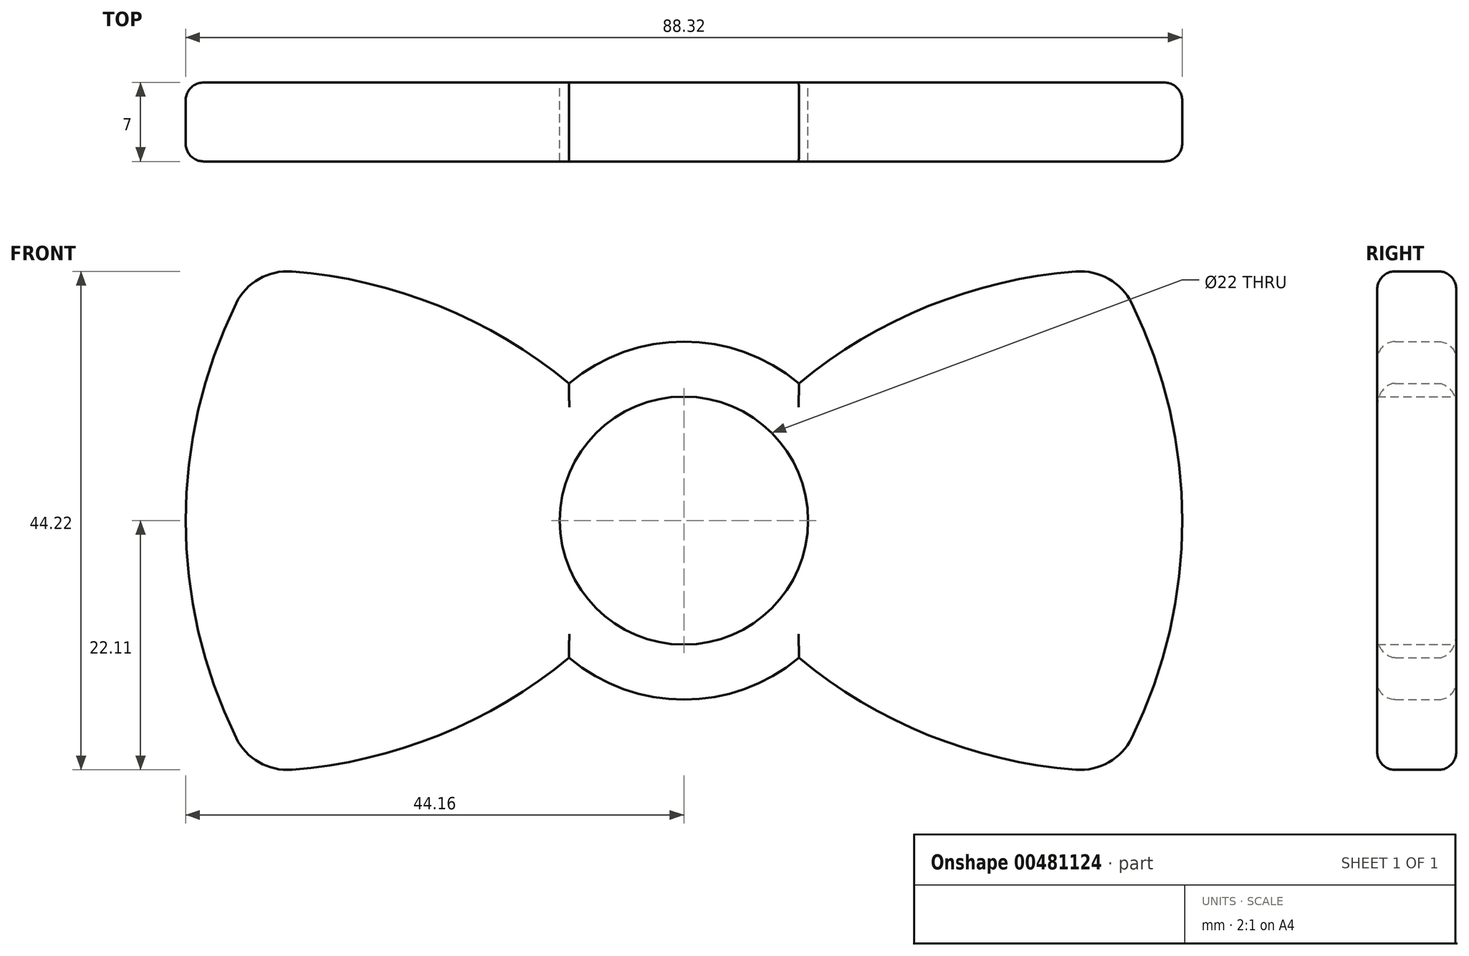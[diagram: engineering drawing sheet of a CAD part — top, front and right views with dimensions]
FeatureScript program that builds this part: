
annotation { "Feature Type Name" : "Feature", "Feature Type Description" : "" }
export const myFeature = defineFeature(function(context is Context, id is Id, definition is map)
    precondition{}
    {
        {
            var Q0;
            Q0=qCreatedBy(makeId("Front.planeOp"),FACE);
            var sketch = newSketch(context, id + "F0", { "sketchPlane" : qUnion([Q0])});
            skLineSegment(sketch, "E0.bottom", {"start": v(38.1, 22.22) * mm, "end": v(-38.1, 22.23) * mm, "construction": true});
            skLineSegment(sketch, "E0.top", {"start": v(38.1, -22.23) * mm, "end": v(-38.1, -22.23) * mm, "construction": true});
            skLineSegment(sketch, "E0.left", {"start": v(38.1, 22.22) * mm, "end": v(38.1, -22.23) * mm});
            skLineSegment(sketch, "E0.right", {"start": v(-38.1, 22.23) * mm, "end": v(-38.1, -22.22) * mm, "construction": true});
            skPoint(sketch, "E0.middle", {"position": v(0, 0) * mm});
            skLineSegment(sketch, "E1", {"start": v(-38.1, 22.23) * mm, "end": v(38.1, -22.23) * mm, "construction": true});
            skLineSegment(sketch, "E2", {"start": v(38.1, 22.23) * mm, "end": v(-38.1, -22.22) * mm, "construction": true});
            skCircle(sketch, "E3", {"center": v(0, 0) * mm, "radius": 15.88 * mm});
            skLineSegment(sketch, "E4", {"start": v(0, 48.06) * mm, "end": v(0, -55.54) * mm, "construction": true});
            skLineSegment(sketch, "E5", {"start": v(-90.95, 0) * mm, "end": v(91.81, 0) * mm, "construction": true});
            skArc(sketch, "E6", {"start": v(-38.1, 22.23) * mm, "mid": v(-44.16, 0) * mm, "end": v(-38.1, -22.23) * mm});
            skArc(sketch, "E7", {"start": v(-38.1, -22.22) * mm, "mid": v(-16.05, -16.26) * mm, "end": v(0, 0) * mm});
            skArc(sketch, "E8", {"start": v(0, 0) * mm, "mid": v(-16.05, 16.26) * mm, "end": v(-38.1, 22.23) * mm});
            skArc(sketch, "E9", {"start": v(38.1, 22.23) * mm, "mid": v(16.05, 16.26) * mm, "end": v(0, 0) * mm});
            skArc(sketch, "E10", {"start": v(38.1, -22.23) * mm, "mid": v(44.16, 0) * mm, "end": v(38.1, 22.22) * mm});
            skArc(sketch, "E11", {"start": v(0, 0) * mm, "mid": v(16.05, -16.26) * mm, "end": v(38.1, -22.23) * mm});
            skSolve(sketch);
        }
        {
            var Q0;
            {var subQ5=sQuery(id+"F0.wireOp",EDGE,"E6");Q0=makeQuery(id+"F0.imprint","IMPRINT",FACE,{"disambiguationData":[TD([[makeQuery(id+"F0.imprint","IMPRINT",EDGE,{"derivedFrom":subQ5}),1.0]])]});}
            var Q1;
            {var subQ0=sQuery(id+"F0.wireOp",EDGE,"E8");var subQ1=sQuery(id+"F0.wireOp",EDGE,"E3");var subQ2=makeQuery(id+"F0.imprint","INTERSECT",VERTEX,{"derivedFrom":[subQ1,subQ0]});Q1=makeQuery(id+"F0.imprint","IMPRINT",FACE,{"disambiguationData":[TD([[makeQuery(id+"F0.imprint","IMPRINT",EDGE,{"disambiguationData":[TD([[subQ2,-1.0]])],"derivedFrom":subQ1}),1.0]])]});}
            var Q2;
            {var subQ0=sQuery(id+"F0.wireOp",EDGE,"E8");var subQ1=sQuery(id+"F0.wireOp",EDGE,"E3");var subQ2=makeQuery(id+"F0.imprint","INTERSECT",VERTEX,{"derivedFrom":[subQ1,subQ0]});Q2=makeQuery(id+"F0.imprint","IMPRINT",FACE,{"disambiguationData":[TD([[makeQuery(id+"F0.imprint","IMPRINT",EDGE,{"disambiguationData":[TD([[subQ2,1.0]])],"derivedFrom":subQ1}),1.0]])]});}
            var Q3;
            {var subQ0=sQuery(id+"F0.wireOp",EDGE,"E7");var subQ1=sQuery(id+"F0.wireOp",EDGE,"E3");var subQ2=makeQuery(id+"F0.imprint","INTERSECT",VERTEX,{"derivedFrom":[subQ1,subQ0]});Q3=makeQuery(id+"F0.imprint","IMPRINT",FACE,{"disambiguationData":[TD([[makeQuery(id+"F0.imprint","IMPRINT",EDGE,{"disambiguationData":[TD([[subQ2,-1.0]])],"derivedFrom":subQ1}),1.0]])]});}
            var Q4;
            {var subQ0=sQuery(id+"F0.wireOp",EDGE,"E9");var subQ1=sQuery(id+"F0.wireOp",EDGE,"E3");var subQ2=makeQuery(id+"F0.imprint","INTERSECT",VERTEX,{"derivedFrom":[subQ1,subQ0]});Q4=makeQuery(id+"F0.imprint","IMPRINT",FACE,{"disambiguationData":[TD([[makeQuery(id+"F0.imprint","IMPRINT",EDGE,{"disambiguationData":[TD([[subQ2,1.0]])],"derivedFrom":subQ1}),1.0]])]});}
            var Q5;
            {var subQ0=sQuery(id+"F0.wireOp",EDGE,"E0.left");Q5=makeQuery(id+"F0.imprint","IMPRINT",FACE,{"disambiguationData":[TD([[makeQuery(id+"F0.imprint","IMPRINT",EDGE,{"derivedFrom":subQ0}),-1.0]])]});}
            var Q6;
            Q6=makeQuery(id+"F0.imprint","IMPRINT",FACE,{"disambiguationData":[TD([[makeQuery(id+"F0.imprint","IMPRINT",EDGE,{"derivedFrom":sQuery(id+"F0.wireOp",EDGE,"E0.left")}),1.0]])]});
            extrude(context, id + "F1", {"entities" : qUnion([Q0, Q1, Q2, Q3, Q4, Q5, Q6]), "depth" : 7 * mm});
        }
        {
            var Q0;
            Q0=makeQuery(id+"F1.opExtrude","CAP_FACE",FACE,{"disambiguationData":[OSD([sQuery(id+"F0.wireOp",EDGE,"E3"),sQuery(id+"F0.wireOp",EDGE,"E6"),sQuery(id+"F0.wireOp",EDGE,"E7"),sQuery(id+"F0.wireOp",EDGE,"E8"),sQuery(id+"F0.wireOp",EDGE,"E9"),sQuery(id+"F0.wireOp",EDGE,"E10"),sQuery(id+"F0.wireOp",EDGE,"E11")])],"isStart":true});
            var sketch = newSketch(context, id + "F2", { "sketchPlane" : qUnion([Q0])});
            skCircle(sketch, "E12", {"center": v(0, 0) * mm, "radius": 11 * mm});
            skLineSegment(sketch, "E13", {"start": v(0, 36.34) * mm, "end": v(0, -37.6) * mm, "construction": true});
            skLineSegment(sketch, "E14", {"start": v(-26.99, 0) * mm, "end": v(26.99, 0) * mm, "construction": true});
            skCircle(sketch, "E15", {"center": v(-26.99, 0) * mm, "radius": 11 * mm});
            skCircle(sketch, "E16", {"center": v(26.99, 0) * mm, "radius": 11 * mm});
            skSolve(sketch);
        }
        {
            var Q0;
            Q0=makeQuery(id+"F2.imprint","IMPRINT",FACE,{"disambiguationData":[TD([[makeQuery(id+"F2.imprint","IMPRINT",EDGE,{"derivedFrom":sQuery(id+"F2.wireOp",EDGE,"E12")}),1.0]])]});
            extrude(context, id + "F3", {"entities" : qUnion([Q0]), "operationType" : NewBodyOperationType.REMOVE, "endBound" : BoundingType.THROUGH_ALL, "oppositeDirection" : true, "depth" : 25.4 * mm});
        }
        {
            var Q0;
            Q0=makeQuery(id+"F1.opExtrude","CAP_EDGE",EDGE,{"disambiguationData":[OSD([sQuery(id+"F0.wireOp",EDGE,"E6")])],"isStart":false});
            var Q1;
            Q1=makeQuery(id+"F1.opExtrude","CAP_EDGE",EDGE,{"disambiguationData":[OSD([sQuery(id+"F0.wireOp",EDGE,"E7")])],"isStart":false});
            var Q2;
            {var subQ0=sQuery(id+"F0.wireOp",EDGE,"E3");Q2=makeQuery(id+"F1.opExtrude","CAP_EDGE",EDGE,{"disambiguationData":[OSD([subQ0]),TDD([makeQuery(id+"F0.imprint","IMPRINT",EDGE,{"disambiguationData":[TD([[makeQuery(id+"F0.imprint","INTERSECT",VERTEX,{"derivedFrom":[subQ0,sQuery(id+"F0.wireOp",EDGE,"E7")]}),-1.0]])],"derivedFrom":subQ0})])],"isStart":false});}
            var Q3;
            Q3=makeQuery(id+"F1.opExtrude","CAP_EDGE",EDGE,{"disambiguationData":[OSD([sQuery(id+"F0.wireOp",EDGE,"E11")])],"isStart":false});
            var Q4;
            Q4=makeQuery(id+"F1.opExtrude","CAP_EDGE",EDGE,{"disambiguationData":[OSD([sQuery(id+"F0.wireOp",EDGE,"E10")])],"isStart":false});
            var Q5;
            Q5=makeQuery(id+"F1.opExtrude","CAP_EDGE",EDGE,{"disambiguationData":[OSD([sQuery(id+"F0.wireOp",EDGE,"E9")])],"isStart":false});
            var Q6;
            {var subQ0=sQuery(id+"F0.wireOp",EDGE,"E3");Q6=makeQuery(id+"F1.opExtrude","CAP_EDGE",EDGE,{"disambiguationData":[OSD([subQ0]),TDD([makeQuery(id+"F0.imprint","IMPRINT",EDGE,{"disambiguationData":[TD([[makeQuery(id+"F0.imprint","INTERSECT",VERTEX,{"derivedFrom":[subQ0,sQuery(id+"F0.wireOp",EDGE,"E8")]}),1.0]])],"derivedFrom":subQ0})])],"isStart":false});}
            var Q7;
            Q7=makeQuery(id+"F1.opExtrude","CAP_EDGE",EDGE,{"disambiguationData":[OSD([sQuery(id+"F0.wireOp",EDGE,"E8")])],"isStart":false});
            var Q8;
            Q8=makeQuery(id+"F1.opExtrude","CAP_EDGE",EDGE,{"disambiguationData":[OSD([sQuery(id+"F0.wireOp",EDGE,"E8")])],"isStart":true});
            var Q9;
            {var subQ0=sQuery(id+"F0.wireOp",EDGE,"E3");Q9=makeQuery(id+"F1.opExtrude","CAP_EDGE",EDGE,{"disambiguationData":[OSD([subQ0]),TDD([makeQuery(id+"F0.imprint","IMPRINT",EDGE,{"disambiguationData":[TD([[makeQuery(id+"F0.imprint","INTERSECT",VERTEX,{"derivedFrom":[subQ0,sQuery(id+"F0.wireOp",EDGE,"E8")]}),1.0]])],"derivedFrom":subQ0})])],"isStart":true});}
            var Q10;
            Q10=makeQuery(id+"F1.opExtrude","CAP_EDGE",EDGE,{"disambiguationData":[OSD([sQuery(id+"F0.wireOp",EDGE,"E9")])],"isStart":true});
            var Q11;
            Q11=makeQuery(id+"F1.opExtrude","CAP_EDGE",EDGE,{"disambiguationData":[OSD([sQuery(id+"F0.wireOp",EDGE,"E10")])],"isStart":true});
            var Q12;
            Q12=makeQuery(id+"F1.opExtrude","CAP_EDGE",EDGE,{"disambiguationData":[OSD([sQuery(id+"F0.wireOp",EDGE,"E11")])],"isStart":true});
            var Q13;
            {var subQ0=sQuery(id+"F0.wireOp",EDGE,"E3");Q13=makeQuery(id+"F1.opExtrude","CAP_EDGE",EDGE,{"disambiguationData":[OSD([subQ0]),TDD([makeQuery(id+"F0.imprint","IMPRINT",EDGE,{"disambiguationData":[TD([[makeQuery(id+"F0.imprint","INTERSECT",VERTEX,{"derivedFrom":[subQ0,sQuery(id+"F0.wireOp",EDGE,"E7")]}),-1.0]])],"derivedFrom":subQ0})])],"isStart":true});}
            var Q14;
            Q14=makeQuery(id+"F1.opExtrude","CAP_EDGE",EDGE,{"disambiguationData":[OSD([sQuery(id+"F0.wireOp",EDGE,"E7")])],"isStart":true});
            var Q15;
            Q15=makeQuery(id+"F1.opExtrude","CAP_EDGE",EDGE,{"disambiguationData":[OSD([sQuery(id+"F0.wireOp",EDGE,"E6")])],"isStart":true});
            fillet(context, id + "F4", {"entities" : qUnion([Q0, Q1, Q2, Q3, Q4, Q5, Q6, Q7, Q8, Q9, Q10, Q11, Q12, Q13, Q14, Q15]), "radius" : 1.59 * mm, "tangentPropagation" : true, "allowEdgeOverflow" : false});
        }
        {
            var Q0;
            Q0=makeQuery(id+"F1.opExtrude","SWEPT_EDGE",EDGE,{"disambiguationData":[OSD([sQuery(id+"F0.wireOp",EDGE,"E6"),sQuery(id+"F0.wireOp",EDGE,"E8")])]});
            var Q1;
            Q1=makeQuery(id+"F1.opExtrude","SWEPT_EDGE",EDGE,{"disambiguationData":[OSD([sQuery(id+"F0.wireOp",EDGE,"E6"),sQuery(id+"F0.wireOp",EDGE,"E7")])]});
            var Q2;
            Q2=makeQuery(id+"F1.opExtrude","SWEPT_EDGE",EDGE,{"disambiguationData":[OSD([sQuery(id+"F0.wireOp",EDGE,"E0.left"),sQuery(id+"F0.wireOp",EDGE,"E9"),sQuery(id+"F0.wireOp",EDGE,"E10")])]});
            var Q3;
            Q3=makeQuery(id+"F1.opExtrude","SWEPT_EDGE",EDGE,{"disambiguationData":[OSD([sQuery(id+"F0.wireOp",EDGE,"E0.left"),sQuery(id+"F0.wireOp",EDGE,"E10"),sQuery(id+"F0.wireOp",EDGE,"E11")])]});
            fillet(context, id + "F5", {"entities" : qUnion([Q0, Q1, Q2, Q3]), "radius" : 5.08 * mm, "tangentPropagation" : true, "allowEdgeOverflow" : false});
        }
    });
